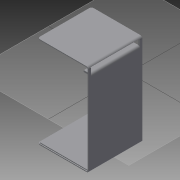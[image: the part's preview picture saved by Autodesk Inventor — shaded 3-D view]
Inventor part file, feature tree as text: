
AUTODESK INVENTOR PART (.ipt)
format: ipt  version: 2015 (Build 190159000, 159)  size: 222,208 bytes
history: native  units: in
note: dims shown in document units (in); Inventor stores cm internally (conversion verified against a paired STEP export)
features: reference x5, other x4, extrude x3, sketch x3, fillet x2, plane x1
ambient origin geometry x8: Origin, YZ Plane, XZ Plane, XY Plane, X Axis, Y Axis, Z Axis, Center Point
bodies: Solid1 (feature_tree)
feature tree (18):
  plane  "Work Plane1"
  extrude  "Extrusion1"  Depth=0.0394in
  other  "Lip1"
  other  "Lip2"
  other  "Lip3"
  other  "Lip4"
  fillet  "Fillet1"  Radius=0.0787in
  fillet  "Fillet2"  Radius=2.4606in
  extrude  "Extrusion2"  Depth=0.0787in
  extrude  "Extrusion3"  Depth=0.1181in
  sketch  "Sketch1"  dims[d1=2.565in d2=0.0in d3=0.0394in]
  reference  "Reference4"
  reference  "Reference5"
  reference  "Reference6"
  reference  "Reference7"
  reference  "Reference8"
  sketch  "Sketch2"  dims[d4=0.0394in d5=0.0394in d6=0.0in d7=0.0in d8=0.0in d9=0.0in d10=0.0394in d11=0.0394in d12=0.0in d13=0.0in d14=0.0in d15=0.0in d17=0.0787in d18=2.4606in]
  sketch  "Sketch3"  dims[d19=4.4882in d20=0.0394in d21=0.0394in d22=0.0in d23=0.0in d24=0.0in d25=0.0in d26=0.0394in d27=0.0394in d28=0.0in d29=0.0in d30=0.0in d31=0.0in d32=0.0787in d33=0.1181in d34=0.1181in d35=0.0in d36=2.4606in d37=0.0in d38=0.1181in d40=0.1181in d41=0.0in d42=0.1181in d43=0.3937in d44=0.0in d45=0.1181in d46=0.3543in d47=0.0787in d48=0.0394in d49=0.1181in d50=2.4075in d51=0.0in]
